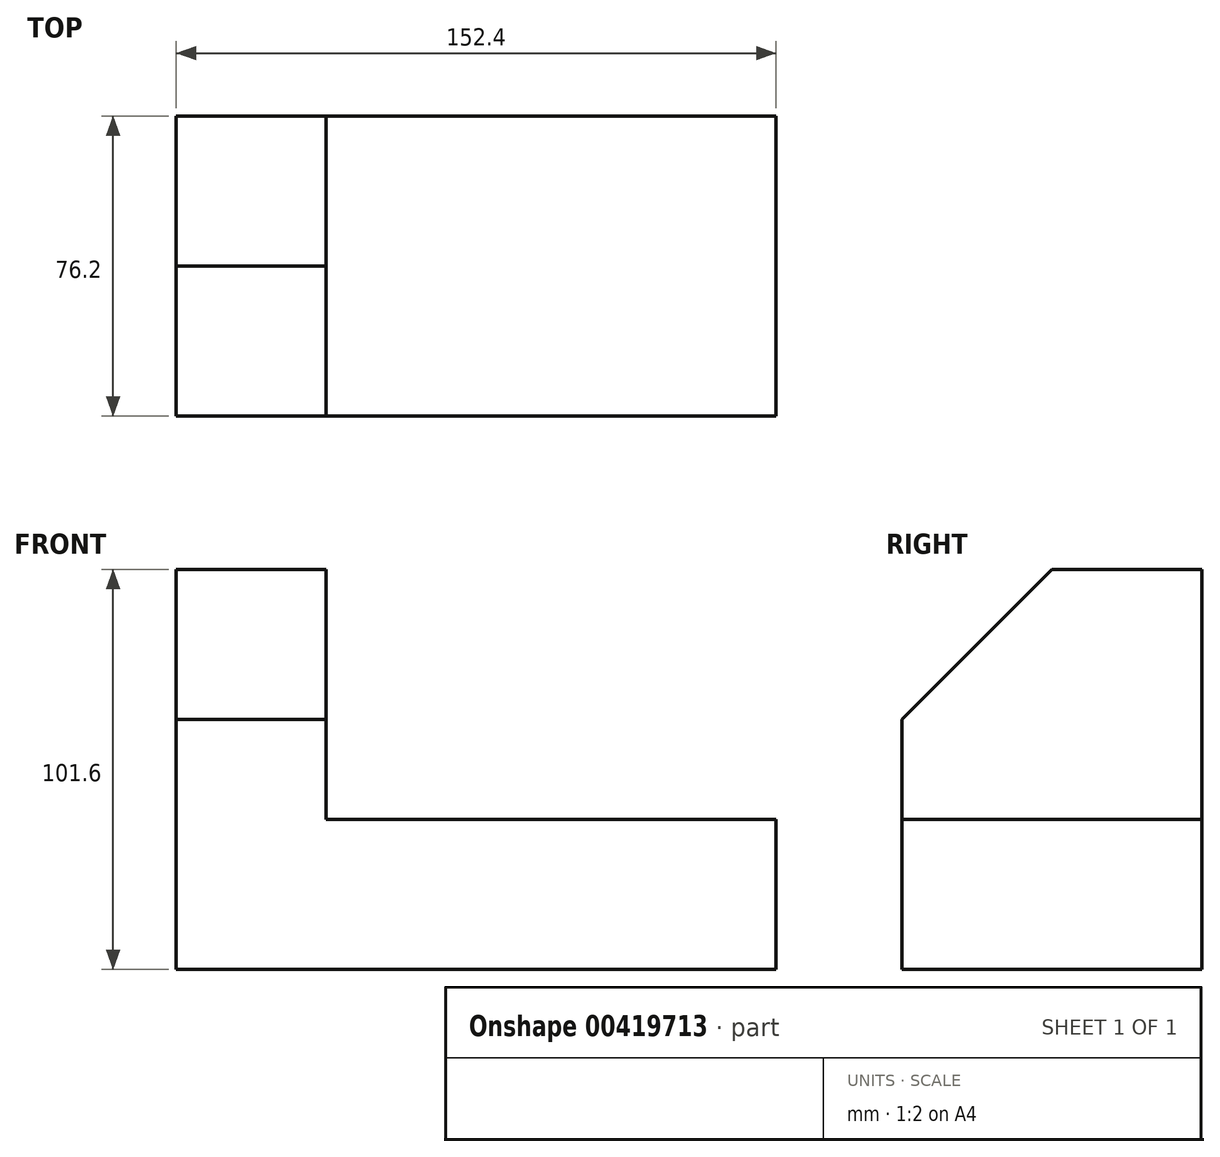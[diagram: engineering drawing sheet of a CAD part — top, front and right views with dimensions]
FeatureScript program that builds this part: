
annotation { "Feature Type Name" : "Feature", "Feature Type Description" : "" }
export const myFeature = defineFeature(function(context is Context, id is Id, definition is map)
    precondition{}
    {
        {
            var Q0;
            Q0=qCreatedBy(makeId("Front.planeOp"),FACE);
            var sketch = newSketch(context, id + "F0", { "sketchPlane" : qUnion([Q0])});
            skLineSegment(sketch, "E0", {"start": v(0, 0) * mm, "end": v(152.4, 0) * mm});
            skLineSegment(sketch, "E1", {"start": v(152.4, 0) * mm, "end": v(152.4, 38.1) * mm});
            skLineSegment(sketch, "E2", {"start": v(152.4, 38.1) * mm, "end": v(38.1, 38.1) * mm});
            skLineSegment(sketch, "E3", {"start": v(38.1, 38.1) * mm, "end": v(38.1, 101.6) * mm});
            skLineSegment(sketch, "E4", {"start": v(38.1, 101.6) * mm, "end": v(0, 101.6) * mm});
            skLineSegment(sketch, "E5", {"start": v(0, 101.6) * mm, "end": v(0, 0) * mm});
            skSolve(sketch);
        }
        {
            var Q0;
            Q0=makeQuery(id+"F0.imprint","IMPRINT",FACE,{"disambiguationData":[TD([[makeQuery(id+"F0.imprint","IMPRINT",EDGE,{"derivedFrom":sQuery(id+"F0.wireOp",EDGE,"E0")}),1.0]])]});
            extrude(context, id + "F1", {"entities" : qUnion([Q0]), "depth" : 76.2 * mm});
        }
        {
            var Q0;
            Q0=makeQuery(id+"F1.opExtrude","SWEPT_FACE",FACE,{"disambiguationData":[OSD([sQuery(id+"F0.wireOp",EDGE,"E3")])]});
            var sketch = newSketch(context, id + "F2", { "sketchPlane" : qUnion([Q0])});
            skLineSegment(sketch, "E6", {"start": v(-38.1, 101.6) * mm, "end": v(-76.2, 63.5) * mm});
            skLineSegment(sketch, "E7", {"start": v(-76.2, 63.5) * mm, "end": v(-76.2, 101.6) * mm});
            skLineSegment(sketch, "E8", {"start": v(-76.2, 101.6) * mm, "end": v(-38.1, 101.6) * mm});
            skSolve(sketch);
        }
        {
            var Q0;
            Q0=makeQuery(id+"F2.imprint","IMPRINT",FACE,{"disambiguationData":[TD([[makeQuery(id+"F2.imprint","IMPRINT",EDGE,{"derivedFrom":sQuery(id+"F2.wireOp",EDGE,"E6")}),-1.0]])]});
            extrude(context, id + "F3", {"entities" : qUnion([Q0]), "operationType" : NewBodyOperationType.REMOVE, "endBound" : BoundingType.THROUGH_ALL, "oppositeDirection" : true, "depth" : 25.4 * mm});
        }
    });
